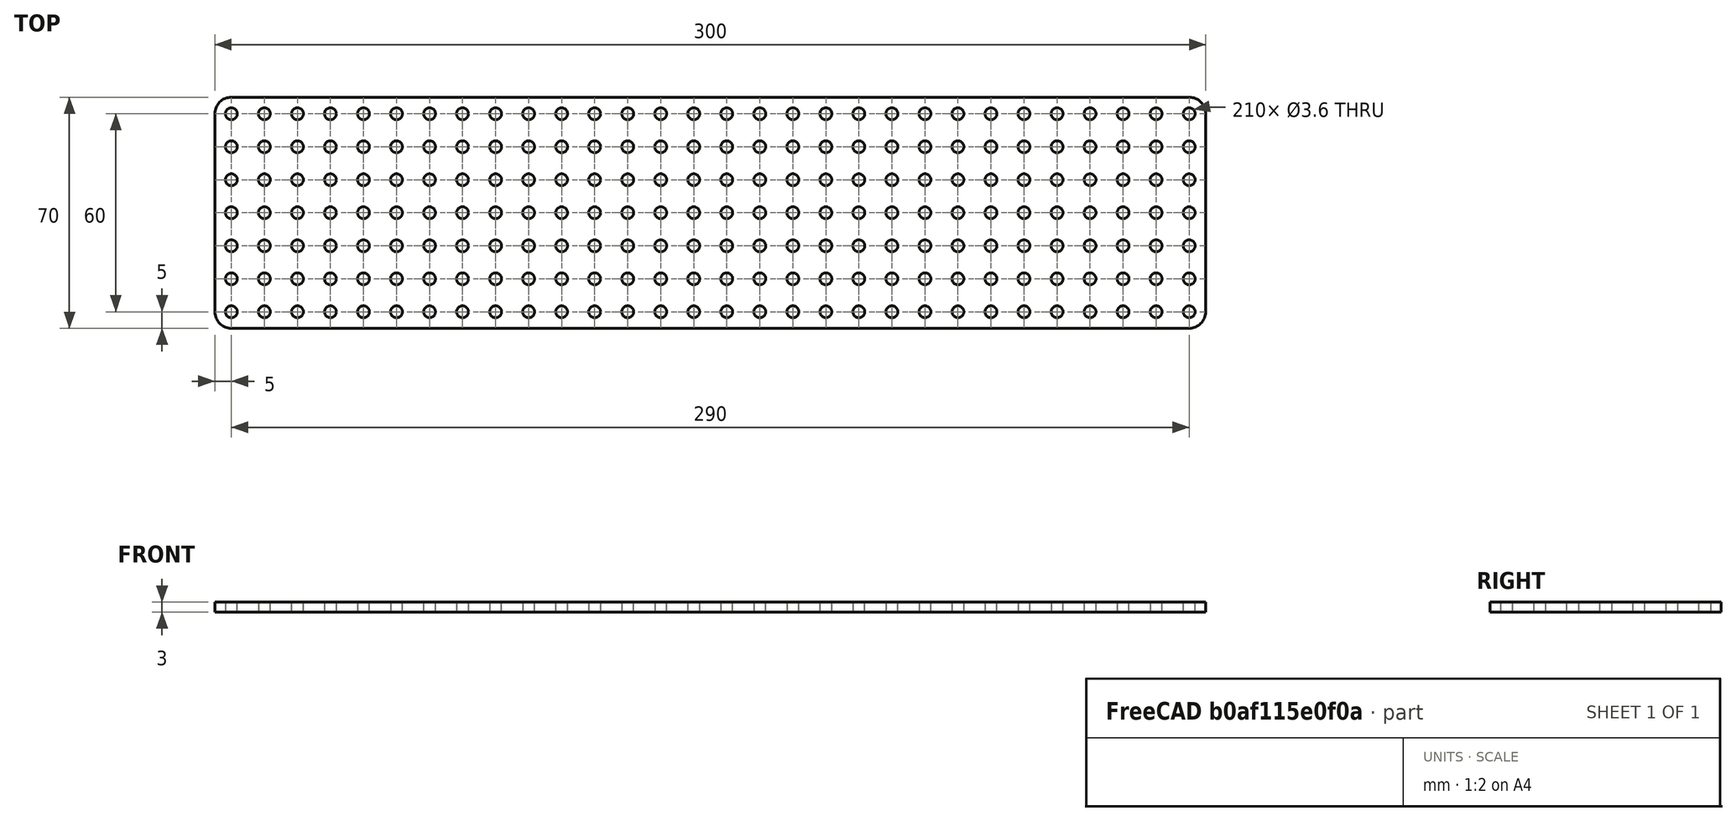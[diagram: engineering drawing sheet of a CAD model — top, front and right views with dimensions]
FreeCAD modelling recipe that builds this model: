
FCSTD DOCUMENT  (FreeCAD 0.20R29410 (Git))
Label: hole_plate30x70
License: All rights reserved
LicenseURL: http://en.wikipedia.org/wiki/All_rights_reserved
objects: Part::FeaturePython×2, Spreadsheet::Sheet×1, Part::Box×1, Part::Cylinder×1, Part::Cut×1, App::Part×1, Part::Fillet×1, TechDraw::DrawSVGTemplate×1, TechDraw::DrawViewPart×1, TechDraw::DrawPage×1, App::DocumentObjectGroup×1
note: 6 computed .brp shape members not serialized (recipe doc carries the construction recipe); baked Part::Feature solids carry a one-line shape summary decoded from their .brp

FEATURE [Spreadsheet::Sheet] Spreadsheet  label="p"
  cells = A1=hole_r; B1(hole_r)=1.8; A2=plate_hole_dist; B2(plate_hole_dist)=10; A3=plate_x; B3(plate_x)=300; A4=plate_y; B4(plate_y)=70
FEATURE [Part::Box] Box  label="hole plate cube"
  AttacherType = Attacher::AttachEngine3D
  Height = 3
  Length = 300
  Width = 70
  expr: Length = <<p>>.plate_x
  expr: Width = <<p>>.plate_y
FEATURE [Part::Cylinder] Cylinder  label="the hole"
  Angle = 360
  AttacherType = Attacher::AttachEngine3D
  FirstAngle = 0
  Height = 10
  Radius = 1.8
  SecondAngle = 0
  expr: Radius = <<p>>.hole_r
FEATURE [Part::FeaturePython] Array  label="hole array"  # Draft array (typed FeaturePython)
  Angle = 360
  ArrayType = 0
  Axis = (0,0,1)
  Base = -> Cylinder
  Center = (0,0,0)
  Fuse = false
  IntervalAxis = (0,0,0)
  IntervalX = (10,0,0)
  IntervalY = (0,10,0)
  IntervalZ = (0,0,1)
  NumberPolar = 1
  NumberX = 30
  NumberY = 7
  NumberZ = 1
  Placement = pos=(5,5,0) rot=(0,0,1;0rad)
  expr: .IntervalX.x = <<p>>.plate_hole_dist
  expr: .Placement.Base.x = <<p>>.plate_hole_dist / 2
  expr: .Placement.Base.y = <<p>>.plate_hole_dist / 2
  expr: NumberX = floor(<<p>>.plate_x / <<p>>.plate_hole_dist)
  expr: NumberY = floor(<<p>>.plate_y / <<p>>.plate_hole_dist)
FEATURE [Part::Cut] Cut  label="hole plate cut"
  Base = -> Box
  Tool = -> Array
FEATURE [App::Part] Part
  Group = -> [Cut]
  Origin = -> Origin
FEATURE [Part::Fillet] Fillet
  Base = -> Cut
  Edges = 4 edges r=5: [Edge1,Edge3,Edge6,Edge221]
FEATURE [TechDraw::DrawSVGTemplate] Template
  Height = 300.4
  Orientation = 0
  Width = 70.6
FEATURE [Part::FeaturePython] LasercutterTechdrawExport  label="Fillet offset"  # WARN: FeaturePython — macro-defined, semantics opaque (R4)
  BeamWidth = 0.2
  Method = 0
  Normal = (0,0,1)
  Part = -> Fillet
  Placement = pos=(0,0,0) rot=(0,0,1;1.5708rad)
FEATURE [TechDraw::DrawViewPart] Fillet_contour
  CoarseView = false
  Direction = (0,0,1)
  Focus = 100
  HardHidden = false
  IsoCount = 0
  IsoHidden = false
  IsoVisible = false
  LockPosition = false
  Perspective = false
  Rotation = 0
  ScaleType = 2
  SeamHidden = false
  SeamVisible = true
  SmoothHidden = false
  SmoothVisible = true
  Source = -> [LasercutterTechdrawExport]
  X = 35.3
  XDirection = (1,0,0)
  Y = 150.1
FEATURE [TechDraw::DrawPage] LasercutterTechdraw
  KeepUpdated = true
  NextBalloonIndex = 1
  ProjectionType = 0
  Template = -> Template
  Views = -> [Fillet_contour]
FEATURE [App::DocumentObjectGroup] LaserCutterExportObjects
  Group = -> [LasercutterTechdrawExport]
